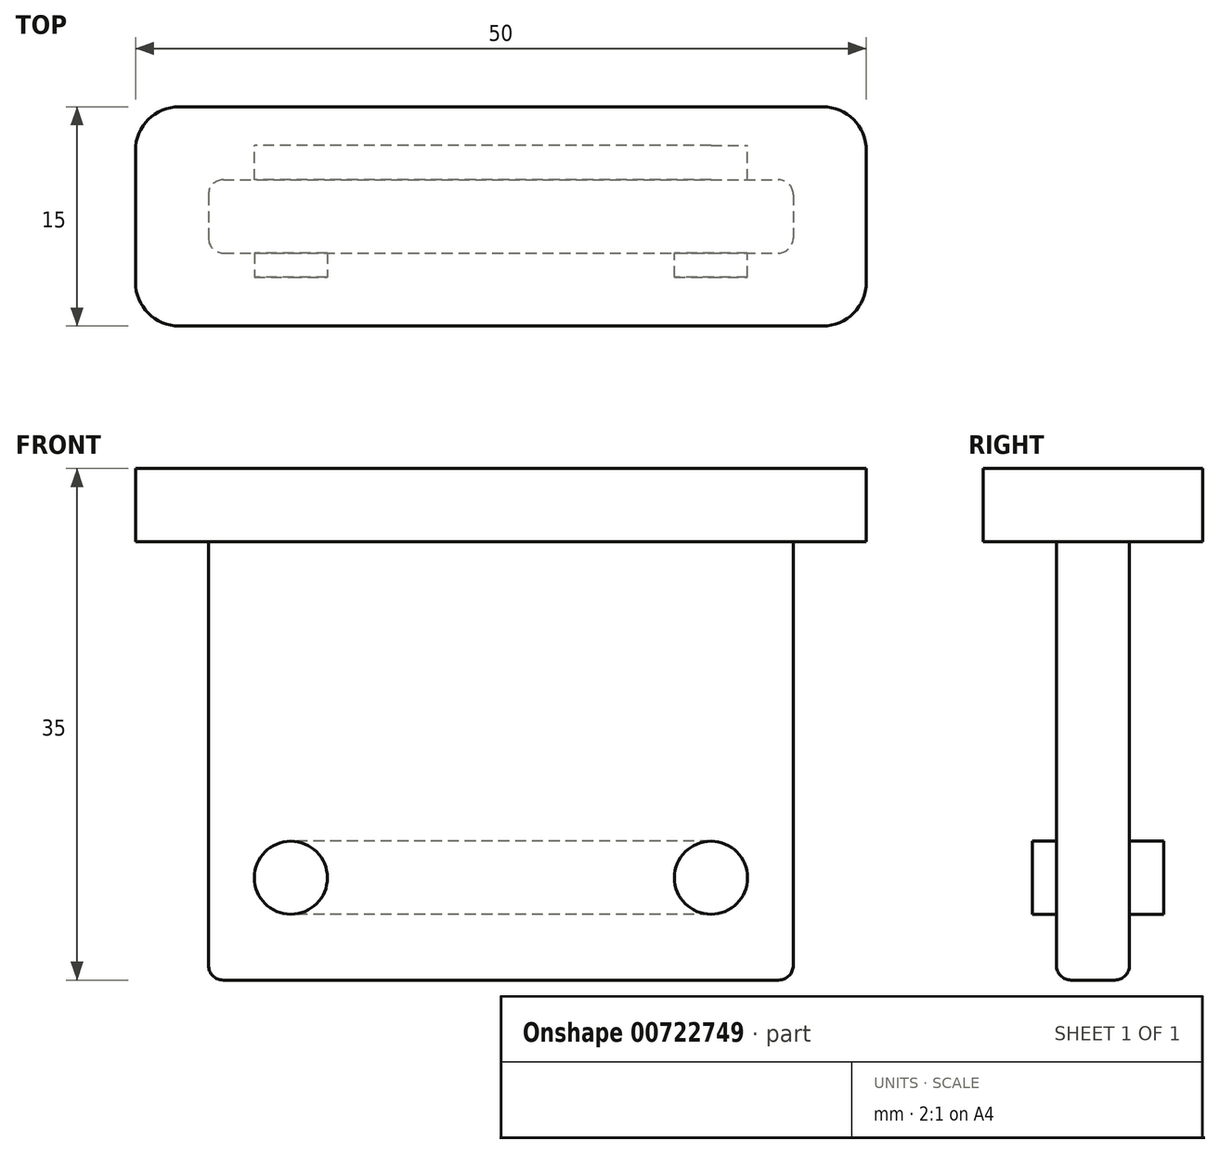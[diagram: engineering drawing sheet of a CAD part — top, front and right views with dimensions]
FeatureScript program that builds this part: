
annotation { "Feature Type Name" : "Feature", "Feature Type Description" : "" }
export const myFeature = defineFeature(function(context is Context, id is Id, definition is map)
    precondition{}
    {
        {
            var Q0;
            Q0=qCreatedBy(makeId("Top.planeOp"),FACE);
            var sketch = newSketch(context, id + "F0", { "sketchPlane" : qUnion([Q0])});
            skLineSegment(sketch, "E0.bottom", {"start": v(-20, 2.5) * mm, "end": v(20, 2.5) * mm});
            skLineSegment(sketch, "E0.top", {"start": v(-20, -2.5) * mm, "end": v(20, -2.5) * mm});
            skLineSegment(sketch, "E0.left", {"start": v(-20, 2.5) * mm, "end": v(-20, -2.5) * mm});
            skLineSegment(sketch, "E0.right", {"start": v(20, 2.5) * mm, "end": v(20, -2.5) * mm});
            skPoint(sketch, "E0.middle", {"position": v(0, 0) * mm});
            skSolve(sketch);
        }
        {
            var Q0;
            Q0 = qSketchRegion(id + "F0", true);
            extrude(context, id + "F1", {"entities" : qUnion([Q0]), "depth" : 30 * mm, "offsetDistance" : 25 * mm});
        }
        {
            var Q0;
            Q0=makeQuery(id+"F1.opExtrude","CAP_FACE",FACE,{"disambiguationData":[OSD([sQuery(id+"F0.wireOp",EDGE,"E0.bottom"),sQuery(id+"F0.wireOp",EDGE,"E0.top"),sQuery(id+"F0.wireOp",EDGE,"E0.left"),sQuery(id+"F0.wireOp",EDGE,"E0.right")])],"isStart":false});
            var sketch = newSketch(context, id + "F2", { "sketchPlane" : qUnion([Q0])});
            skLineSegment(sketch, "E1.bottom", {"start": v(-25, 7.5) * mm, "end": v(25, 7.5) * mm});
            skLineSegment(sketch, "E1.top", {"start": v(-25, -7.5) * mm, "end": v(25, -7.5) * mm});
            skLineSegment(sketch, "E1.left", {"start": v(-25, 7.5) * mm, "end": v(-25, -7.5) * mm});
            skLineSegment(sketch, "E1.right", {"start": v(25, 7.5) * mm, "end": v(25, -7.5) * mm});
            skPoint(sketch, "E1.middle", {"position": v(0, 0) * mm});
            skSolve(sketch);
        }
        {
            var Q0;
            Q0 = qSketchRegion(id + "F2", true);
            extrude(context, id + "F3", {"entities" : qUnion([Q0]), "operationType" : NewBodyOperationType.ADD, "depth" : 5 * mm, "offsetDistance" : 25 * mm});
        }
        {
            var Q0;
            Q0=makeQuery(id+"F1.opExtrude","SWEPT_EDGE",EDGE,{"disambiguationData":[OSD([sQuery(id+"F0.wireOp",EDGE,"E0.bottom"),sQuery(id+"F0.wireOp",EDGE,"E0.right")])]});
            var Q1;
            Q1=makeQuery(id+"F1.opExtrude","SWEPT_EDGE",EDGE,{"disambiguationData":[OSD([sQuery(id+"F0.wireOp",EDGE,"E0.top"),sQuery(id+"F0.wireOp",EDGE,"E0.right")])]});
            var Q2;
            Q2=makeQuery(id+"F1.opExtrude","SWEPT_EDGE",EDGE,{"disambiguationData":[OSD([sQuery(id+"F0.wireOp",EDGE,"E0.top"),sQuery(id+"F0.wireOp",EDGE,"E0.left")])]});
            var Q3;
            Q3=makeQuery(id+"F1.opExtrude","SWEPT_EDGE",EDGE,{"disambiguationData":[OSD([sQuery(id+"F0.wireOp",EDGE,"E0.bottom"),sQuery(id+"F0.wireOp",EDGE,"E0.left")])]});
            var Q4;
            Q4=makeQuery(id+"F1.opExtrude","CAP_EDGE",EDGE,{"disambiguationData":[OSD([sQuery(id+"F0.wireOp",EDGE,"E0.bottom")])],"isStart":true});
            var Q5;
            Q5=makeQuery(id+"F1.opExtrude","CAP_EDGE",EDGE,{"disambiguationData":[OSD([sQuery(id+"F0.wireOp",EDGE,"E0.top")])],"isStart":true});
            var Q6;
            Q6=makeQuery(id+"F1.opExtrude","CAP_EDGE",EDGE,{"disambiguationData":[OSD([sQuery(id+"F0.wireOp",EDGE,"E0.right")])],"isStart":true});
            var Q7;
            Q7=makeQuery(id+"F1.opExtrude","CAP_EDGE",EDGE,{"disambiguationData":[OSD([sQuery(id+"F0.wireOp",EDGE,"E0.left")])],"isStart":true});
            fillet(context, id + "F4", {"entities" : qUnion([Q0, Q1, Q2, Q3, Q4, Q5, Q6, Q7]), "radius" : 1 * mm, "tangentPropagation" : true, "allowEdgeOverflow" : false});
        }
        {
            var Q0;
            Q0=makeQuery(id+"F3.opExtrude","SWEPT_EDGE",EDGE,{"disambiguationData":[OSD([sQuery(id+"F2.wireOp",EDGE,"E1.bottom"),sQuery(id+"F2.wireOp",EDGE,"E1.right")])]});
            var Q1;
            Q1=makeQuery(id+"F3.opExtrude","SWEPT_EDGE",EDGE,{"disambiguationData":[OSD([sQuery(id+"F2.wireOp",EDGE,"E1.top"),sQuery(id+"F2.wireOp",EDGE,"E1.right")])]});
            var Q2;
            Q2=makeQuery(id+"F3.opExtrude","SWEPT_EDGE",EDGE,{"disambiguationData":[OSD([sQuery(id+"F2.wireOp",EDGE,"E1.bottom"),sQuery(id+"F2.wireOp",EDGE,"E1.left")])]});
            var Q3;
            Q3=makeQuery(id+"F3.opExtrude","SWEPT_EDGE",EDGE,{"disambiguationData":[OSD([sQuery(id+"F2.wireOp",EDGE,"E1.top"),sQuery(id+"F2.wireOp",EDGE,"E1.left")])]});
            fillet(context, id + "F5", {"entities" : qUnion([Q0, Q1, Q2, Q3]), "radius" : 3 * mm, "tangentPropagation" : true, "allowEdgeOverflow" : false});
        }
        {
            var Q0;
            Q0=makeQuery(id+"F3.opExtrude","CAP_FACE",FACE,{"disambiguationData":[OSD([sQuery(id+"F2.wireOp",EDGE,"E1.bottom"),sQuery(id+"F2.wireOp",EDGE,"E1.top"),sQuery(id+"F2.wireOp",EDGE,"E1.left"),sQuery(id+"F2.wireOp",EDGE,"E1.right")])],"isStart":true});
            cPlane(context, id + "F6", {"entities" : qUnion([Q0]), "cplaneType" : CPlaneType.OFFSET, "offset" : 20.5 * mm, "width" : 150 * mm, "height" : 150 * mm});
        }
        {
            var Q0;
            Q0=qCreatedBy(id+"F6.planeOp",FACE);
            var sketch = newSketch(context, id + "F7", { "sketchPlane" : qUnion([Q0])});
            skLineSegment(sketch, "E2", {"start": v(21.87, 0) * mm, "end": v(16.87, 0) * mm, "construction": true});
            skLineSegment(sketch, "E3", {"start": v(16.87, 0) * mm, "end": v(16.87, -2.5) * mm, "construction": true});
            skLineSegment(sketch, "E4.bottom", {"start": v(16.87, -4.85) * mm, "end": v(11.87, -4.85) * mm});
            skLineSegment(sketch, "E4.top", {"start": v(16.87, 4.15) * mm, "end": v(11.87, 4.15) * mm});
            skLineSegment(sketch, "E4.left", {"start": v(16.87, -4.85) * mm, "end": v(16.87, 4.15) * mm});
            skLineSegment(sketch, "E4.right", {"start": v(11.87, -4.85) * mm, "end": v(11.87, 4.15) * mm});
            skLineSegment(sketch, "E5.bottom", {"start": v(11.87, -2.5) * mm, "end": v(0, -2.5) * mm});
            skLineSegment(sketch, "E5.top", {"start": v(11.87, -4.85) * mm, "end": v(0, -4.85) * mm});
            skLineSegment(sketch, "E5.right", {"start": v(0, -2.5) * mm, "end": v(0, -4.85) * mm});
            skSolve(sketch);
        }
        {
            var Q0;
            Q0 = qSketchRegion(id + "F7", true);
            extrude(context, id + "F8", {"entities" : qUnion([Q0]), "depth" : 5 * mm, "offsetDistance" : 25 * mm});
        }
        {
            var Q0;
            Q0=makeQuery(id+"F8.opExtrude","SWEPT_BODY",BODY,{"disambiguationData":[OSD([sQuery(id+"F7.wireOp",EDGE,"E4.bottom"),sQuery(id+"F7.wireOp",EDGE,"E4.top"),sQuery(id+"F7.wireOp",EDGE,"E4.left"),sQuery(id+"F7.wireOp",EDGE,"E4.right"),sQuery(id+"F7.wireOp",EDGE,"E5.bottom"),sQuery(id+"F7.wireOp",EDGE,"E5.top"),sQuery(id+"F7.wireOp",EDGE,"E5.right")])]});
            var Q1;
            Q1=qCreatedBy(makeId("Right.planeOp"),FACE);
            mirror(context, id + "F9", {"operationType" : NewBodyOperationType.ADD, "entities" : qUnion([Q0]), "mirrorPlane" : qUnion([Q1])});
        }
        {
            var Q0;
            Q0=makeQuery(id+"F9.opPattern","COPY",EDGE,{"derivedFrom":makeQuery(id+"F8.opExtrude","CAP_EDGE",EDGE,{"disambiguationData":[OSD([sQuery(id+"F7.wireOp",EDGE,"E4.left")])],"isStart":false}),"instanceName":"1"});
            var Q1;
            Q1=makeQuery(id+"F9.opPattern","COPY",EDGE,{"derivedFrom":makeQuery(id+"F8.opExtrude","CAP_EDGE",EDGE,{"disambiguationData":[OSD([sQuery(id+"F7.wireOp",EDGE,"E4.right")])],"isStart":false}),"instanceName":"1"});
            var Q2;
            Q2=makeQuery(id+"F8.opExtrude","CAP_EDGE",EDGE,{"disambiguationData":[OSD([sQuery(id+"F7.wireOp",EDGE,"E4.right")])],"isStart":false});
            var Q3;
            Q3=makeQuery(id+"F8.opExtrude","CAP_EDGE",EDGE,{"disambiguationData":[OSD([sQuery(id+"F7.wireOp",EDGE,"E4.left")])],"isStart":false});
            var Q4;
            Q4=makeQuery(id+"F8.opExtrude","CAP_EDGE",EDGE,{"disambiguationData":[OSD([sQuery(id+"F7.wireOp",EDGE,"E4.left")])],"isStart":true});
            var Q5;
            Q5=makeQuery(id+"F9.opPattern","COPY",EDGE,{"derivedFrom":makeQuery(id+"F8.opExtrude","CAP_EDGE",EDGE,{"disambiguationData":[OSD([sQuery(id+"F7.wireOp",EDGE,"E4.right")])],"isStart":true}),"instanceName":"1"});
            var Q6;
            Q6=makeQuery(id+"F8.opExtrude","CAP_EDGE",EDGE,{"disambiguationData":[OSD([sQuery(id+"F7.wireOp",EDGE,"E4.right")])],"isStart":true});
            var Q7;
            Q7=makeQuery(id+"F9.opPattern","COPY",EDGE,{"derivedFrom":makeQuery(id+"F8.opExtrude","CAP_EDGE",EDGE,{"disambiguationData":[OSD([sQuery(id+"F7.wireOp",EDGE,"E4.left")])],"isStart":true}),"instanceName":"1"});
            fillet(context, id + "F10", {"entities" : qUnion([Q0, Q1, Q2, Q3, Q4, Q5, Q6, Q7]), "radius" : 2.5 * mm, "tangentPropagation" : true, "allowEdgeOverflow" : false});
        }
    });
